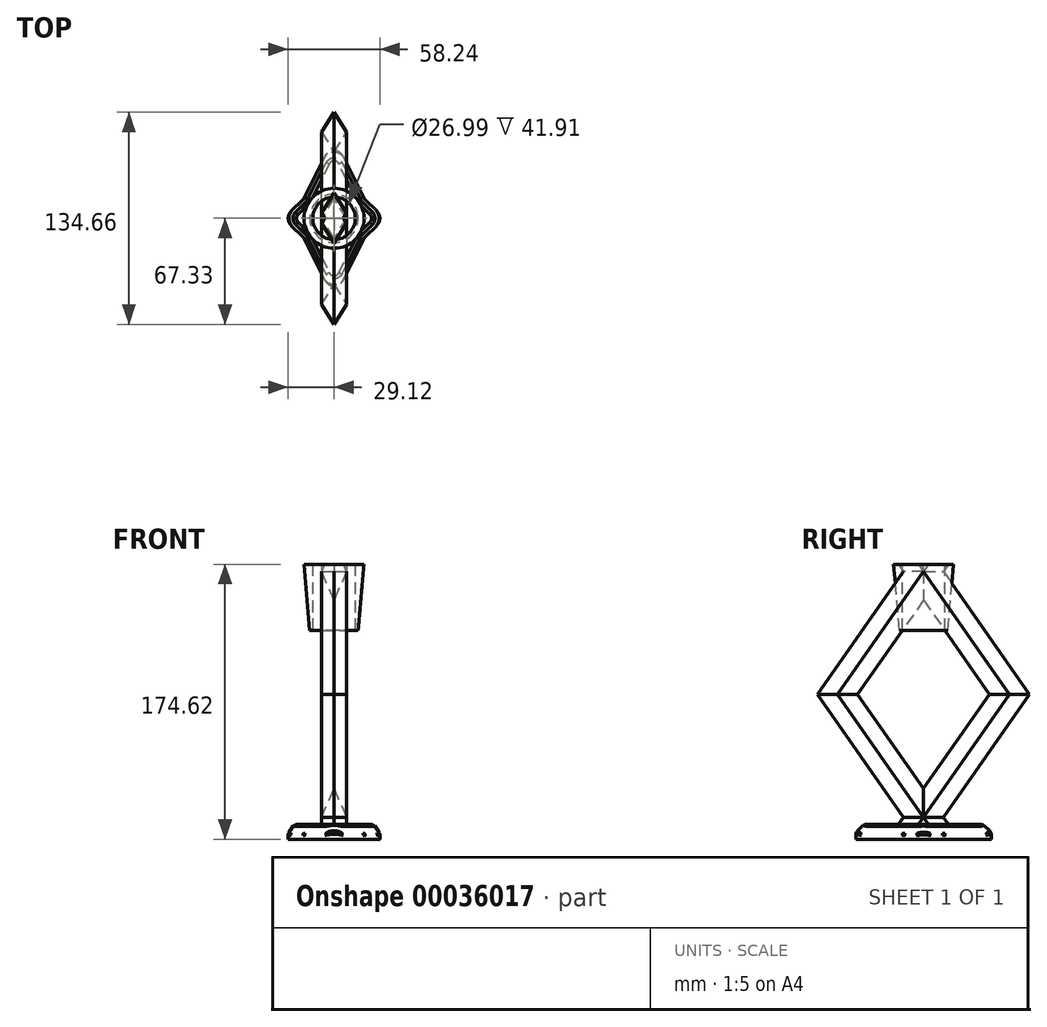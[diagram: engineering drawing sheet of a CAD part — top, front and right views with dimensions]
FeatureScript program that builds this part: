
annotation { "Feature Type Name" : "Feature", "Feature Type Description" : "" }
export const myFeature = defineFeature(function(context is Context, id is Id, definition is map)
    precondition{}
    {
        {
            var Q0;
            Q0=qCreatedBy(makeId("Top.planeOp"),FACE);
            var sketch = newSketch(context, id + "F0", { "sketchPlane" : qUnion([Q0])});
            skLineSegment(sketch, "E0", {"start": v(0, 50.8) * mm, "end": v(19.05, 12.7) * mm});
            skLineSegment(sketch, "E1", {"start": v(19.05, 12.7) * mm, "end": v(31.75, 0) * mm});
            skLineSegment(sketch, "E2", {"start": v(31.75, 0) * mm, "end": v(0, 0) * mm, "construction": true});
            skLineSegment(sketch, "E3", {"start": v(0, 0) * mm, "end": v(0, 50.8) * mm, "construction": true});
            skLineSegment(sketch, "E4.MirrorCS", {"start": v(-19.05, 12.7) * mm, "end": v(-31.75, 0) * mm});
            skLineSegment(sketch, "E5.MirrorCS", {"start": v(0, 50.8) * mm, "end": v(-19.05, 12.7) * mm});
            skLineSegment(sketch, "E6.MirrorCS", {"start": v(-19.05, -12.7) * mm, "end": v(-31.75, 0) * mm});
            skLineSegment(sketch, "E7.MirrorCS", {"start": v(19.05, -12.7) * mm, "end": v(31.75, 0) * mm});
            skLineSegment(sketch, "E8.MirrorCS", {"start": v(0, -50.8) * mm, "end": v(19.05, -12.7) * mm});
            skLineSegment(sketch, "E9.MirrorCS", {"start": v(0, -50.8) * mm, "end": v(-19.05, -12.7) * mm});
            skSolve(sketch);
        }
        {
            var Q0;
            Q0 = qSketchRegion(id + "F0", true);
            extrude(context, id + "F1", {"entities" : qUnion([Q0]), "depth" : 6.35 * mm, "hasDraft" : true, "draftAngle" : 25 * degree, "draftPullDirection" : true});
        }
        {
            var Q0;
            Q0 = qSketchRegion(id + "F0", true);
            extrude(context, id + "F2", {"entities" : qUnion([Q0]), "operationType" : NewBodyOperationType.ADD, "oppositeDirection" : true, "depth" : 3.17 * mm});
        }
        {
            var Q0;
            Q0=makeQuery(id+"F1.opExtrude","SWEPT_EDGE",EDGE,{"disambiguationData":[OSD([sQuery(id+"F0.wireOp",EDGE,"E0"),sQuery(id+"F0.wireOp",EDGE,"E5.MirrorCS")])]});
            var Q1;
            Q1=makeQuery(id+"F1.opExtrude","SWEPT_EDGE",EDGE,{"disambiguationData":[OSD([sQuery(id+"F0.wireOp",EDGE,"E0"),sQuery(id+"F0.wireOp",EDGE,"E1")])]});
            var Q2;
            Q2=makeQuery(id+"F1.opExtrude","SWEPT_EDGE",EDGE,{"disambiguationData":[OSD([sQuery(id+"F0.wireOp",EDGE,"E4.MirrorCS"),sQuery(id+"F0.wireOp",EDGE,"E6.MirrorCS")])]});
            var Q3;
            Q3=makeQuery(id+"F1.opExtrude","SWEPT_EDGE",EDGE,{"disambiguationData":[OSD([sQuery(id+"F0.wireOp",EDGE,"E1"),sQuery(id+"F0.wireOp",EDGE,"E7.MirrorCS")])]});
            var Q4;
            Q4=makeQuery(id+"F1.opExtrude","SWEPT_EDGE",EDGE,{"disambiguationData":[OSD([sQuery(id+"F0.wireOp",EDGE,"E4.MirrorCS"),sQuery(id+"F0.wireOp",EDGE,"E5.MirrorCS")])]});
            var Q5;
            Q5=makeQuery(id+"F1.opExtrude","SWEPT_EDGE",EDGE,{"disambiguationData":[OSD([sQuery(id+"F0.wireOp",EDGE,"E6.MirrorCS"),sQuery(id+"F0.wireOp",EDGE,"E9.MirrorCS")])]});
            var Q6;
            Q6=makeQuery(id+"F1.opExtrude","SWEPT_EDGE",EDGE,{"disambiguationData":[OSD([sQuery(id+"F0.wireOp",EDGE,"E8.MirrorCS"),sQuery(id+"F0.wireOp",EDGE,"E9.MirrorCS")])]});
            var Q7;
            Q7=makeQuery(id+"F1.opExtrude","SWEPT_EDGE",EDGE,{"disambiguationData":[OSD([sQuery(id+"F0.wireOp",EDGE,"E7.MirrorCS"),sQuery(id+"F0.wireOp",EDGE,"E8.MirrorCS")])]});
            var Q8;
            Q8=makeQuery(id+"F2.opExtrude","SWEPT_EDGE",EDGE,{"disambiguationData":[OSD([sQuery(id+"F0.wireOp",EDGE,"E8.MirrorCS"),sQuery(id+"F0.wireOp",EDGE,"E9.MirrorCS")])]});
            var Q9;
            Q9=makeQuery(id+"F2.opExtrude","SWEPT_EDGE",EDGE,{"disambiguationData":[OSD([sQuery(id+"F0.wireOp",EDGE,"E7.MirrorCS"),sQuery(id+"F0.wireOp",EDGE,"E8.MirrorCS")])]});
            var Q10;
            Q10=makeQuery(id+"F2.opExtrude","SWEPT_EDGE",EDGE,{"disambiguationData":[OSD([sQuery(id+"F0.wireOp",EDGE,"E1"),sQuery(id+"F0.wireOp",EDGE,"E7.MirrorCS")])]});
            var Q11;
            Q11=makeQuery(id+"F2.opExtrude","SWEPT_EDGE",EDGE,{"disambiguationData":[OSD([sQuery(id+"F0.wireOp",EDGE,"E6.MirrorCS"),sQuery(id+"F0.wireOp",EDGE,"E9.MirrorCS")])]});
            var Q12;
            Q12=makeQuery(id+"F2.opExtrude","SWEPT_EDGE",EDGE,{"disambiguationData":[OSD([sQuery(id+"F0.wireOp",EDGE,"E4.MirrorCS"),sQuery(id+"F0.wireOp",EDGE,"E6.MirrorCS")])]});
            var Q13;
            Q13=makeQuery(id+"F2.opExtrude","SWEPT_EDGE",EDGE,{"disambiguationData":[OSD([sQuery(id+"F0.wireOp",EDGE,"E0"),sQuery(id+"F0.wireOp",EDGE,"E1")])]});
            var Q14;
            Q14=makeQuery(id+"F2.opExtrude","SWEPT_EDGE",EDGE,{"disambiguationData":[OSD([sQuery(id+"F0.wireOp",EDGE,"E0"),sQuery(id+"F0.wireOp",EDGE,"E5.MirrorCS")])]});
            var Q15;
            Q15=makeQuery(id+"F2.opExtrude","SWEPT_EDGE",EDGE,{"disambiguationData":[OSD([sQuery(id+"F0.wireOp",EDGE,"E4.MirrorCS"),sQuery(id+"F0.wireOp",EDGE,"E5.MirrorCS")])]});
            fillet(context, id + "F3", {"entities" : qUnion([Q0, Q1, Q2, Q3, Q4, Q5, Q6, Q7, Q8, Q9, Q10, Q11, Q12, Q13, Q14, Q15]), "radius" : 6.35 * mm, "tangentPropagation" : true, "allowEdgeOverflow" : false});
        }
        {
            var Q0;
            {var subQ0=sQuery(id+"F0.wireOp",EDGE,"E0");Q0=makeQuery(id+"F2.boolean.opBoolean","MERGE",EDGE,{"derivedFrom":[makeQuery(id+"F1.opExtrude","CAP_EDGE",EDGE,{"disambiguationData":[OSD([subQ0])],"isStart":true}),makeQuery(id+"F2.opExtrude","CAP_EDGE",EDGE,{"disambiguationData":[OSD([subQ0])],"isStart":true})]});}
            var Q1;
            {var subQ0=sQuery(id+"F0.wireOp",EDGE,"E1");Q1=makeQuery(id+"F2.boolean.opBoolean","MERGE",EDGE,{"derivedFrom":[makeQuery(id+"F1.opExtrude","CAP_EDGE",EDGE,{"disambiguationData":[OSD([subQ0])],"isStart":true}),makeQuery(id+"F2.opExtrude","CAP_EDGE",EDGE,{"disambiguationData":[OSD([subQ0])],"isStart":true})]});}
            var Q2;
            {var subQ0=sQuery(id+"F0.wireOp",EDGE,"E5.MirrorCS");Q2=makeQuery(id+"F2.boolean.opBoolean","MERGE",EDGE,{"derivedFrom":[makeQuery(id+"F1.opExtrude","CAP_EDGE",EDGE,{"disambiguationData":[OSD([subQ0])],"isStart":true}),makeQuery(id+"F2.opExtrude","CAP_EDGE",EDGE,{"disambiguationData":[OSD([subQ0])],"isStart":true})]});}
            var Q3;
            {var subQ0=sQuery(id+"F0.wireOp",EDGE,"E4.MirrorCS");Q3=makeQuery(id+"F2.boolean.opBoolean","MERGE",EDGE,{"derivedFrom":[makeQuery(id+"F1.opExtrude","CAP_EDGE",EDGE,{"disambiguationData":[OSD([subQ0])],"isStart":true}),makeQuery(id+"F2.opExtrude","CAP_EDGE",EDGE,{"disambiguationData":[OSD([subQ0])],"isStart":true})]});}
            var Q4;
            {var subQ0=sQuery(id+"F0.wireOp",EDGE,"E6.MirrorCS");Q4=makeQuery(id+"F2.boolean.opBoolean","MERGE",EDGE,{"derivedFrom":[makeQuery(id+"F1.opExtrude","CAP_EDGE",EDGE,{"disambiguationData":[OSD([subQ0])],"isStart":true}),makeQuery(id+"F2.opExtrude","CAP_EDGE",EDGE,{"disambiguationData":[OSD([subQ0])],"isStart":true})]});}
            var Q5;
            {var subQ0=sQuery(id+"F0.wireOp",EDGE,"E9.MirrorCS");Q5=makeQuery(id+"F2.boolean.opBoolean","MERGE",EDGE,{"derivedFrom":[makeQuery(id+"F1.opExtrude","CAP_EDGE",EDGE,{"disambiguationData":[OSD([subQ0])],"isStart":true}),makeQuery(id+"F2.opExtrude","CAP_EDGE",EDGE,{"disambiguationData":[OSD([subQ0])],"isStart":true})]});}
            var Q6;
            {var subQ0=sQuery(id+"F0.wireOp",EDGE,"E8.MirrorCS");Q6=makeQuery(id+"F2.boolean.opBoolean","MERGE",EDGE,{"derivedFrom":[makeQuery(id+"F1.opExtrude","CAP_EDGE",EDGE,{"disambiguationData":[OSD([subQ0])],"isStart":true}),makeQuery(id+"F2.opExtrude","CAP_EDGE",EDGE,{"disambiguationData":[OSD([subQ0])],"isStart":true})]});}
            var Q7;
            {var subQ0=sQuery(id+"F0.wireOp",EDGE,"E7.MirrorCS");Q7=makeQuery(id+"F2.boolean.opBoolean","MERGE",EDGE,{"derivedFrom":[makeQuery(id+"F1.opExtrude","CAP_EDGE",EDGE,{"disambiguationData":[OSD([subQ0])],"isStart":true}),makeQuery(id+"F2.opExtrude","CAP_EDGE",EDGE,{"disambiguationData":[OSD([subQ0])],"isStart":true})]});}
            fillet(context, id + "F4", {"entities" : qUnion([Q0, Q1, Q2, Q3, Q4, Q5, Q6, Q7]), "radius" : 3.17 * mm, "tangentPropagation" : true, "allowEdgeOverflow" : false});
        }
        {
            var Q0;
            Q0=makeQuery(id+"F1.opExtrude","CAP_EDGE",EDGE,{"disambiguationData":[OSD([sQuery(id+"F0.wireOp",EDGE,"E9.MirrorCS")])],"isStart":false});
            chamfer(context, id + "F5", {"entities" : qUnion([Q0]), "width" : 2.54 * mm, "tangentPropagation" : true});
        }
        {
            var Q0;
            Q0=makeQuery(id+"F1.opExtrude","CAP_FACE",FACE,{"disambiguationData":[OSD([sQuery(id+"F0.wireOp",EDGE,"E0"),sQuery(id+"F0.wireOp",EDGE,"E1"),sQuery(id+"F0.wireOp",EDGE,"E4.MirrorCS"),sQuery(id+"F0.wireOp",EDGE,"E5.MirrorCS"),sQuery(id+"F0.wireOp",EDGE,"E6.MirrorCS"),sQuery(id+"F0.wireOp",EDGE,"E7.MirrorCS"),sQuery(id+"F0.wireOp",EDGE,"E8.MirrorCS"),sQuery(id+"F0.wireOp",EDGE,"E9.MirrorCS")])],"isStart":false});
            var sketch = newSketch(context, id + "F6", { "sketchPlane" : qUnion([Q0])});
            skLineSegment(sketch, "E10", {"start": v(0, 15.88) * mm, "end": v(7.94, 3.17) * mm});
            skLineSegment(sketch, "E11", {"start": v(7.94, 3.17) * mm, "end": v(0, -9.52) * mm});
            skLineSegment(sketch, "E12", {"start": v(0, -9.53) * mm, "end": v(-7.94, 3.17) * mm});
            skLineSegment(sketch, "E13", {"start": v(-7.94, 3.17) * mm, "end": v(0, 15.88) * mm});
            skSolve(sketch);
        }
        {
            var Q0;
            Q0=qCreatedBy(makeId("Right.planeOp"),FACE);
            var sketch = newSketch(context, id + "F7", { "sketchPlane" : qUnion([Q0])});
            skLineSegment(sketch, "E14", {"start": v(-9.53, 6.35) * mm, "end": v(-67.33, 88.9) * mm});
            skSolve(sketch);
        }
        {
            var Q0;
            Q0 = qSketchRegion(id + "F6", true);
            var Q1;
            Q1 = qConstructionFilter(qBodyType(qCreatedBy(id + "F7" ,EDGE), BodyType.WIRE), ConstructionObject.NO);
            sweep(context, id + "F8", {"profiles" : qUnion([Q0]), "path" : qUnion([Q1])});
        }
        {
            var Q0;
            Q0=makeQuery(id+"F8.opSweep","SWEPT_BODY",BODY,{"disambiguationData":[OSD([sQuery(id+"F6.wireOp",EDGE,"E10"),sQuery(id+"F6.wireOp",EDGE,"E11"),sQuery(id+"F6.wireOp",EDGE,"E12"),sQuery(id+"F6.wireOp",EDGE,"E13"),sQuery(id+"F7.wireOp",EDGE,"E14")])]});
            var Q1;
            Q1=qCreatedBy(makeId("Front.planeOp"),FACE);
            mirror(context, id + "F9", {"entities" : qUnion([Q0]), "mirrorPlane" : qUnion([Q1])});
        }
        {
            var Q0;
            Q0=makeQuery(id+"F8.opSweep","SWEPT_BODY",BODY,{"disambiguationData":[OSD([sQuery(id+"F6.wireOp",EDGE,"E10"),sQuery(id+"F6.wireOp",EDGE,"E11"),sQuery(id+"F6.wireOp",EDGE,"E12"),sQuery(id+"F6.wireOp",EDGE,"E13"),sQuery(id+"F7.wireOp",EDGE,"E14")])]});
            var Q1;
            Q1=makeQuery(id+"F9.opPattern","COPY",BODY,{"derivedFrom":makeQuery(id+"F8.opSweep","SWEPT_BODY",BODY,{"disambiguationData":[OSD([sQuery(id+"F6.wireOp",EDGE,"E10"),sQuery(id+"F6.wireOp",EDGE,"E11"),sQuery(id+"F6.wireOp",EDGE,"E12"),sQuery(id+"F6.wireOp",EDGE,"E13"),sQuery(id+"F7.wireOp",EDGE,"E14")])]}),"instanceName":"1"});
            var Q2;
            Q2=makeQuery(id+"F9.opPattern","COPY",FACE,{"derivedFrom":makeQuery(id+"F8.opSweep","CAP_FACE",FACE,{"disambiguationData":[OSD([sQuery(id+"F6.wireOp",EDGE,"E10"),sQuery(id+"F6.wireOp",EDGE,"E11"),sQuery(id+"F6.wireOp",EDGE,"E12"),sQuery(id+"F6.wireOp",EDGE,"E13"),sQuery(id+"F7.wireOp",VERTEX,"E14.end")])],"isStart":false}),"instanceName":"1"});
            mirror(context, id + "F10", {"entities" : qUnion([Q0, Q1]), "mirrorPlane" : qUnion([Q2])});
        }
        {
            var Q0;
            Q0=qCreatedBy(makeId("Right.planeOp"),FACE);
            var sketch = newSketch(context, id + "F11", { "sketchPlane" : qUnion([Q0])});
            skLineSegment(sketch, "E15", {"start": v(-3.17, 6.35) * mm, "end": v(3.17, 6.35) * mm});
            skLineSegment(sketch, "E16", {"start": v(3.18, 6.35) * mm, "end": v(0, 10.88) * mm});
            skLineSegment(sketch, "E17", {"start": v(0, 10.88) * mm, "end": v(-3.17, 6.35) * mm});
            skSolve(sketch);
        }
        {
            var Q0;
            Q0 = qSketchRegion(id + "F11", true);
            extrude(context, id + "F12", {"entities" : qUnion([Q0]), "depth" : 7.94 * mm, "hasSecondDirection" : true, "secondDirectionOppositeDirection" : true, "secondDirectionDepth" : 7.94 * mm});
        }
        {
            var Q0;
            Q0=makeQuery(id+"F10.opPattern","COPY",FACE,{"derivedFrom":makeQuery(id+"F8.opSweep","CAP_FACE",FACE,{"disambiguationData":[OSD([sQuery(id+"F6.wireOp",EDGE,"E10"),sQuery(id+"F6.wireOp",EDGE,"E11"),sQuery(id+"F6.wireOp",EDGE,"E12"),sQuery(id+"F6.wireOp",EDGE,"E13"),sQuery(id+"F7.wireOp",VERTEX,"E14.start")])],"isStart":true}),"instanceName":"1"});
            var sketch = newSketch(context, id + "F13", { "sketchPlane" : qUnion([Q0])});
            skCircle(sketch, "E18", {"center": v(0, 0) * mm, "radius": 15.88 * mm, "construction": true});
            skCircle(sketch, "E19", {"center": v(0, 0) * mm, "radius": 13.5 * mm});
            skSolve(sketch);
        }
        {
            var Q0;
            Q0 = qSketchRegion(id + "F13", true);
            extrude(context, id + "F14", {"entities" : qUnion([Q0]), "oppositeDirection" : true, "depth" : 127 * mm});
        }
        {
            var Q0;
            Q0=makeQuery(id+"F14.opExtrude","CAP_EDGE",EDGE,{"disambiguationData":[OSD([sQuery(id+"F13.wireOp",EDGE,"E19")])],"isStart":false});
            fillet(context, id + "F15", {"entities" : qUnion([Q0]), "radius" : 12.7 * mm, "tangentPropagation" : true, "allowEdgeOverflow" : false});
        }
        {
            var Q0;
            Q0=makeQuery(id+"F1.opExtrude","SWEPT_BODY",BODY,{"disambiguationData":[OSD([sQuery(id+"F0.wireOp",EDGE,"E0"),sQuery(id+"F0.wireOp",EDGE,"E1"),sQuery(id+"F0.wireOp",EDGE,"E4.MirrorCS"),sQuery(id+"F0.wireOp",EDGE,"E5.MirrorCS"),sQuery(id+"F0.wireOp",EDGE,"E6.MirrorCS"),sQuery(id+"F0.wireOp",EDGE,"E7.MirrorCS"),sQuery(id+"F0.wireOp",EDGE,"E8.MirrorCS"),sQuery(id+"F0.wireOp",EDGE,"E9.MirrorCS")])]});
            var Q1;
            Q1=makeQuery(id+"F8.opSweep","SWEPT_BODY",BODY,{"disambiguationData":[OSD([sQuery(id+"F6.wireOp",EDGE,"E10"),sQuery(id+"F6.wireOp",EDGE,"E11"),sQuery(id+"F6.wireOp",EDGE,"E12"),sQuery(id+"F6.wireOp",EDGE,"E13"),sQuery(id+"F7.wireOp",EDGE,"E14")])]});
            var Q2;
            Q2=makeQuery(id+"F9.opPattern","COPY",BODY,{"derivedFrom":makeQuery(id+"F8.opSweep","SWEPT_BODY",BODY,{"disambiguationData":[OSD([sQuery(id+"F6.wireOp",EDGE,"E10"),sQuery(id+"F6.wireOp",EDGE,"E11"),sQuery(id+"F6.wireOp",EDGE,"E12"),sQuery(id+"F6.wireOp",EDGE,"E13"),sQuery(id+"F7.wireOp",EDGE,"E14")])]}),"instanceName":"1"});
            var Q3;
            Q3=makeQuery(id+"F10.opPattern","COPY",BODY,{"derivedFrom":makeQuery(id+"F8.opSweep","SWEPT_BODY",BODY,{"disambiguationData":[OSD([sQuery(id+"F6.wireOp",EDGE,"E10"),sQuery(id+"F6.wireOp",EDGE,"E11"),sQuery(id+"F6.wireOp",EDGE,"E12"),sQuery(id+"F6.wireOp",EDGE,"E13"),sQuery(id+"F7.wireOp",EDGE,"E14")])]}),"instanceName":"1"});
            var Q4;
            Q4=makeQuery(id+"F10.opPattern","COPY",BODY,{"derivedFrom":makeQuery(id+"F9.opPattern","COPY",BODY,{"derivedFrom":makeQuery(id+"F8.opSweep","SWEPT_BODY",BODY,{"disambiguationData":[OSD([sQuery(id+"F6.wireOp",EDGE,"E10"),sQuery(id+"F6.wireOp",EDGE,"E11"),sQuery(id+"F6.wireOp",EDGE,"E12"),sQuery(id+"F6.wireOp",EDGE,"E13"),sQuery(id+"F7.wireOp",EDGE,"E14")])]}),"instanceName":"1"}),"instanceName":"1"});
            var Q5;
            Q5=makeQuery(id+"F12.opExtrude","SWEPT_BODY",BODY,{"disambiguationData":[OSD([sQuery(id+"F11.wireOp",EDGE,"E15"),sQuery(id+"F11.wireOp",EDGE,"E16"),sQuery(id+"F11.wireOp",EDGE,"E17")])]});
            booleanBodies(context, id + "F16", {"operationType" : BooleanOperationType.UNION, "tools" : qUnion([Q0, Q1, Q2, Q3, Q4, Q5])});
        }
        {
            var Q0;
            {var subQ0=makeQuery(id+"F8.opSweep","CAP_FACE",FACE,{"disambiguationData":[OSD([sQuery(id+"F6.wireOp",EDGE,"E10"),sQuery(id+"F6.wireOp",EDGE,"E11"),sQuery(id+"F6.wireOp",EDGE,"E12"),sQuery(id+"F6.wireOp",EDGE,"E13"),sQuery(id+"F7.wireOp",VERTEX,"E14.start")])],"isStart":true});Q0=makeQuery(id+"F16.opBoolean","MERGE",FACE,{"derivedFrom":[makeQuery(id+"F10.opPattern","COPY",FACE,{"derivedFrom":subQ0,"instanceName":"1"}),makeQuery(id+"F10.opPattern","COPY",FACE,{"derivedFrom":makeQuery(id+"F9.opPattern","COPY",FACE,{"derivedFrom":subQ0,"instanceName":"1"}),"instanceName":"1"})]});}
            var sketch = newSketch(context, id + "F17", { "sketchPlane" : qUnion([Q0])});
            skCircle(sketch, "E20", {"center": v(0, 0) * mm, "radius": 19.05 * mm});
            skSolve(sketch);
        }
        {
            var Q0;
            Q0 = qSketchRegion(id + "F17", true);
            extrude(context, id + "F18", {"entities" : qUnion([Q0]), "oppositeDirection" : true, "depth" : 41.9 * mm, "hasDraft" : true, "draftAngle" : 5 * degree, "draftPullDirection" : true});
        }
        {
            var Q0;
            Q0=makeQuery(id+"F14.opExtrude","SWEPT_BODY",BODY,{"disambiguationData":[OSD([sQuery(id+"F13.wireOp",EDGE,"E19")])]});
            var Q1;
            Q1=makeQuery(id+"F18.opExtrude","SWEPT_BODY",BODY,{"disambiguationData":[OSD([sQuery(id+"F17.wireOp",EDGE,"E20")])]});
            booleanBodies(context, id + "F19", {"operationType" : BooleanOperationType.SUBTRACTION, "tools" : qUnion([Q0]), "targets" : qUnion([Q1])});
        }
    });
